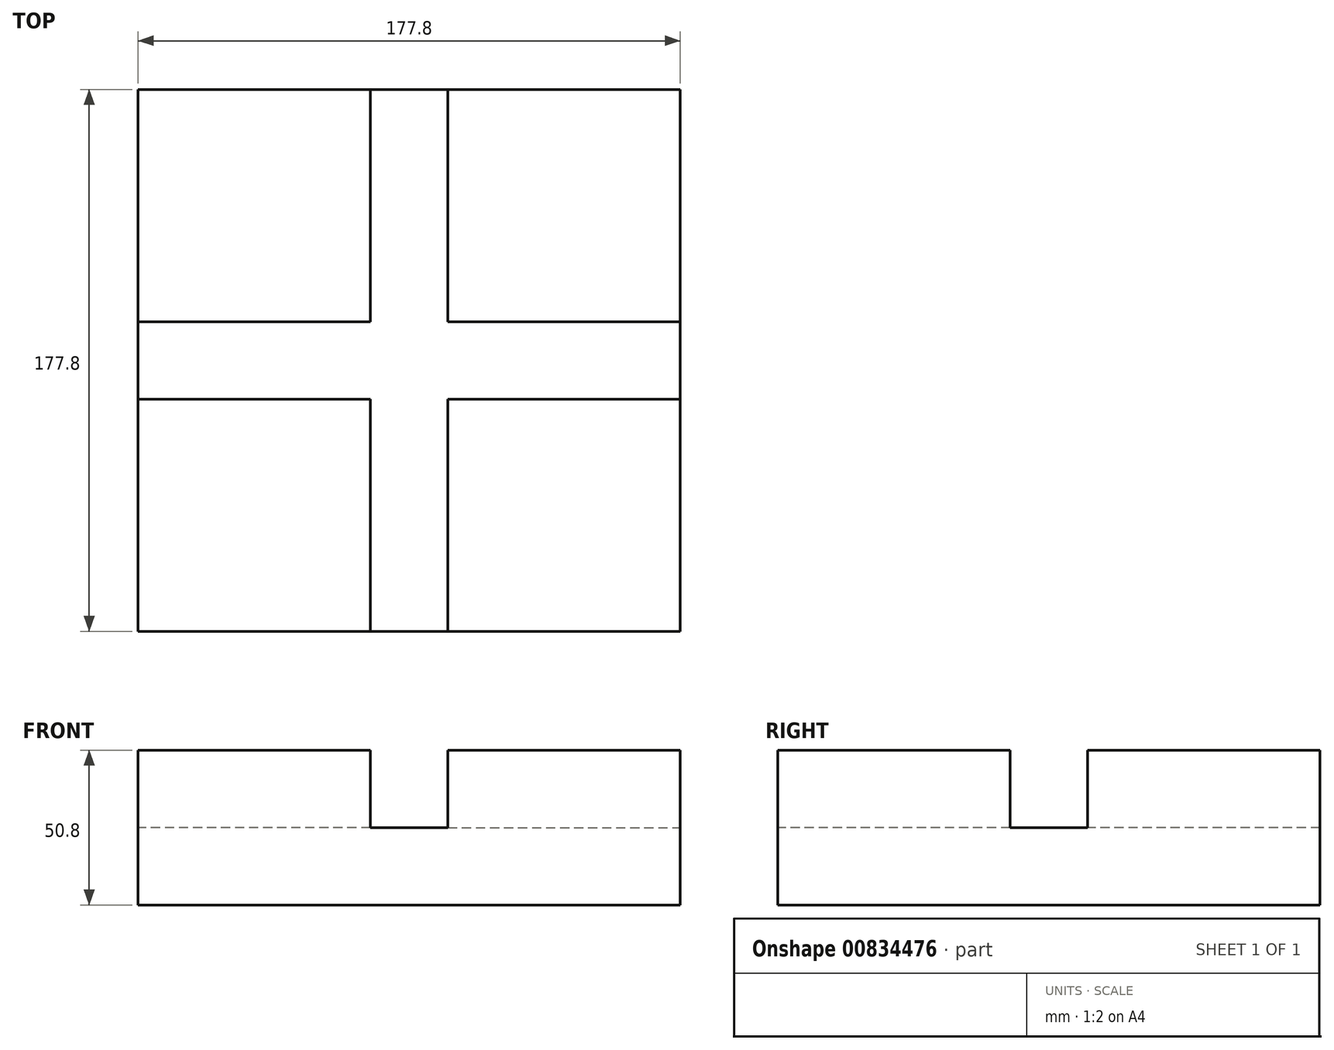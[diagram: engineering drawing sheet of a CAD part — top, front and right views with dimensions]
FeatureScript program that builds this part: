
annotation { "Feature Type Name" : "Feature", "Feature Type Description" : "" }
export const myFeature = defineFeature(function(context is Context, id is Id, definition is map)
    precondition{}
    {
        {
            var Q0;
            Q0=qCreatedBy(makeId("Top.planeOp"),FACE);
            var sketch = newSketch(context, id + "F0", { "sketchPlane" : qUnion([Q0])});
            skLineSegment(sketch, "E0.bottom", {"start": v(-64.66, 68.1) * mm, "end": v(62.34, 68.1) * mm});
            skLineSegment(sketch, "E0.top", {"start": v(-64.66, -58.9) * mm, "end": v(62.34, -58.9) * mm});
            skLineSegment(sketch, "E0.left", {"start": v(-64.66, 68.1) * mm, "end": v(-64.66, -58.9) * mm});
            skLineSegment(sketch, "E0.right", {"start": v(62.34, 68.1) * mm, "end": v(62.34, -58.9) * mm});
            skSolve(sketch);
        }
        {
            var Q0;
            Q0=makeQuery(id+"F0.imprint","IMPRINT",FACE,{"disambiguationData":[TD([[makeQuery(id+"F0.imprint","IMPRINT",EDGE,{"derivedFrom":sQuery(id+"F0.wireOp",EDGE,"E0.bottom")}),-1.0]])]});
            extrude(context, id + "F1", {"entities" : qUnion([Q0]), "depth" : 50.8 * mm, "offsetDistance" : 25.4 * mm});
        }
        {
            var Q0;
            Q0=makeQuery(id+"F1.opExtrude","CAP_FACE",FACE,{"disambiguationData":[OSD([sQuery(id+"F0.wireOp",EDGE,"E0.bottom"),sQuery(id+"F0.wireOp",EDGE,"E0.top"),sQuery(id+"F0.wireOp",EDGE,"E0.left"),sQuery(id+"F0.wireOp",EDGE,"E0.right")])],"isStart":false});
            var sketch = newSketch(context, id + "F2", { "sketchPlane" : qUnion([Q0])});
            skLineSegment(sketch, "E1", {"start": v(-13.86, 68.1) * mm, "end": v(-13.86, 17.3) * mm});
            skLineSegment(sketch, "E2", {"start": v(-13.86, 17.3) * mm, "end": v(-64.66, 17.3) * mm});
            skLineSegment(sketch, "E3", {"start": v(-64.66, 17.3) * mm, "end": v(-64.66, -8.1) * mm});
            skLineSegment(sketch, "E4", {"start": v(-64.66, -8.1) * mm, "end": v(-13.86, -8.1) * mm});
            skLineSegment(sketch, "E5", {"start": v(-13.86, -8.1) * mm, "end": v(-13.86, -58.9) * mm});
            skLineSegment(sketch, "E6", {"start": v(-13.86, -58.9) * mm, "end": v(11.54, -58.9) * mm});
            skLineSegment(sketch, "E7", {"start": v(11.54, -58.9) * mm, "end": v(11.54, -8.1) * mm});
            skLineSegment(sketch, "E8", {"start": v(11.54, -8.1) * mm, "end": v(62.34, -8.1) * mm});
            skLineSegment(sketch, "E9", {"start": v(62.34, -8.1) * mm, "end": v(62.34, 17.3) * mm});
            skLineSegment(sketch, "E10", {"start": v(62.34, 17.3) * mm, "end": v(11.54, 17.3) * mm});
            skLineSegment(sketch, "E11", {"start": v(11.54, 17.3) * mm, "end": v(11.54, 68.1) * mm});
            skLineSegment(sketch, "E12", {"start": v(11.54, 68.1) * mm, "end": v(-13.86, 68.1) * mm});
            skSolve(sketch);
        }
        {
            var Q0;
            Q0=makeQuery(id+"F2.imprint","IMPRINT",FACE,{"disambiguationData":[TD([[makeQuery(id+"F2.imprint","IMPRINT",EDGE,{"derivedFrom":sQuery(id+"F2.wireOp",EDGE,"E1")}),1.0]])]});
            extrude(context, id + "F3", {"entities" : qUnion([Q0]), "operationType" : NewBodyOperationType.REMOVE, "oppositeDirection" : true, "depth" : 25.4 * mm, "offsetDistance" : 25.4 * mm});
        }
        {
            var Q0;
            Q0=makeQuery(id+"F1.opExtrude","SWEPT_FACE",FACE,{"disambiguationData":[OSD([sQuery(id+"F0.wireOp",EDGE,"E0.top")])]});
            extrude(context, id + "F4", {"entities" : qUnion([Q0]), "operationType" : NewBodyOperationType.ADD, "depth" : 25.4 * mm, "offsetDistance" : 25.4 * mm});
        }
        {
            var Q0;
            {var subQ0=sQuery(id+"F0.wireOp",EDGE,"E0.right");Q0=makeQuery(id+"F4.boolean.opBoolean","MERGE",FACE,{"derivedFrom":[makeQuery(id+"F1.opExtrude","SWEPT_FACE",FACE,{"disambiguationData":[OSD([subQ0])]}),makeQuery(id+"F4.opExtrude","SWEPT_FACE",FACE,{"disambiguationData":[OSD([sQuery(id+"F0.wireOp",EDGE,"E0.top"),subQ0])]})]});}
            extrude(context, id + "F5", {"entities" : qUnion([Q0]), "operationType" : NewBodyOperationType.ADD, "depth" : 25.4 * mm, "offsetDistance" : 25.4 * mm});
        }
        {
            var Q0;
            {var subQ0=sQuery(id+"F0.wireOp",EDGE,"E0.bottom");Q0=makeQuery(id+"F5.boolean.opBoolean","MERGE",FACE,{"derivedFrom":[makeQuery(id+"F1.opExtrude","SWEPT_FACE",FACE,{"disambiguationData":[OSD([subQ0])]}),makeQuery(id+"F5.opExtrude","SWEPT_FACE",FACE,{"disambiguationData":[OSD([subQ0,sQuery(id+"F0.wireOp",EDGE,"E0.right")])]})]});}
            extrude(context, id + "F6", {"entities" : qUnion([Q0]), "operationType" : NewBodyOperationType.ADD, "depth" : 25.4 * mm, "offsetDistance" : 25.4 * mm});
        }
        {
            var Q0;
            {var subQ0=sQuery(id+"F0.wireOp",EDGE,"E0.left");Q0=makeQuery(id+"F6.boolean.opBoolean","MERGE",FACE,{"derivedFrom":[makeQuery(id+"F4.boolean.opBoolean","MERGE",FACE,{"derivedFrom":[makeQuery(id+"F1.opExtrude","SWEPT_FACE",FACE,{"disambiguationData":[OSD([subQ0])]}),makeQuery(id+"F4.opExtrude","SWEPT_FACE",FACE,{"disambiguationData":[OSD([sQuery(id+"F0.wireOp",EDGE,"E0.top"),subQ0])]})]}),makeQuery(id+"F6.opExtrude","SWEPT_FACE",FACE,{"disambiguationData":[OSD([sQuery(id+"F0.wireOp",EDGE,"E0.bottom"),subQ0])]})]});}
            extrude(context, id + "F7", {"entities" : qUnion([Q0]), "operationType" : NewBodyOperationType.ADD, "depth" : 25.4 * mm, "offsetDistance" : 25.4 * mm});
        }
    });
